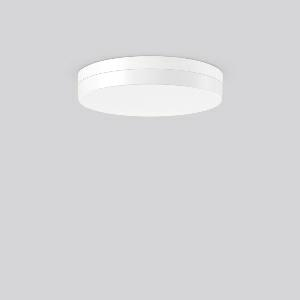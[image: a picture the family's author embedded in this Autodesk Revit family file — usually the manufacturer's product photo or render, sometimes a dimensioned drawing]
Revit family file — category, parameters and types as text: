
# Revit family: flat_slim_round_312632_002_01c9
name_source: partatom
category: Lighting Fixtures
units: mm (PartAtom-declared; Revit-internal decimal feet)

## family parameters
Cut with Voids When Loaded = No
Host = Face
Light Source = No
Part Type = Normal
Room Calculation Point = No
Round Connector Dimension = Use Diameter
Shared = No

## types (1)
- MultiLumen 1 830 (1 x LED Modul 830, 2400 lm, 3000)
    Apparent Load = 20 VA
    CIE Flux Codes = 39 70 90 83 100
    Color Rendering = 80
    Color Temperature = 3000
    Default Elevation = 1800 mm
    Height = 70 mm
    Lamp = 1 x LED Modul 830
    Lamp Light Flux = 2400 lm
    Lamp count = 1
    Length = 400 mm
    Lifetime = 50000 h
    Luminous efficacy = 120 lm/W
    Manufacturer = RZB
    ModVariant = No
    Model = 312632.002
    Mounting Place = Ceiling
    Mounting Type = Surface mounted
    Number of Poles = 1
    OnlyDefault = Yes
    Power Factor = 1
    Product Name = FLAT SLIM round
    Product group = Surface mounted ceiling and wall luminaires
    ProductGroupID = 305
    Protection Class = Protection class I
    Protection Degree = Degree of protection
    RLX_Detail_Level = 1
    RLX_Emergency_Light_Flux = 0 lm
    RLX_Emergency_Type = 0
    RLX_Emergency_Type_DB = No
    RlxData = <blob elided: 19889 chars, md5=52c4d640>
    Socket = socket
    Standby Power = 0 W
    System Light Flux = 2400 lm
    System Power = 20 W
    Type Comments = MultiLumen 1 830
    Type Image = 312631.002.jpg
    URL = http://relux.com
    VarID = multilumen_1_830
    Voltage = 0 V
    Weight = 0.00 kg
    Width = 0 mm  [stored 0 ft]

note: [stored X ft] marks values corroborated as IEEE doubles in the binary element streams (Revit-internal decimal feet)

## geometry (parser evidence)
native form markers: Blend x4, Sweep x12
no freeform markers — native parametric forms only
